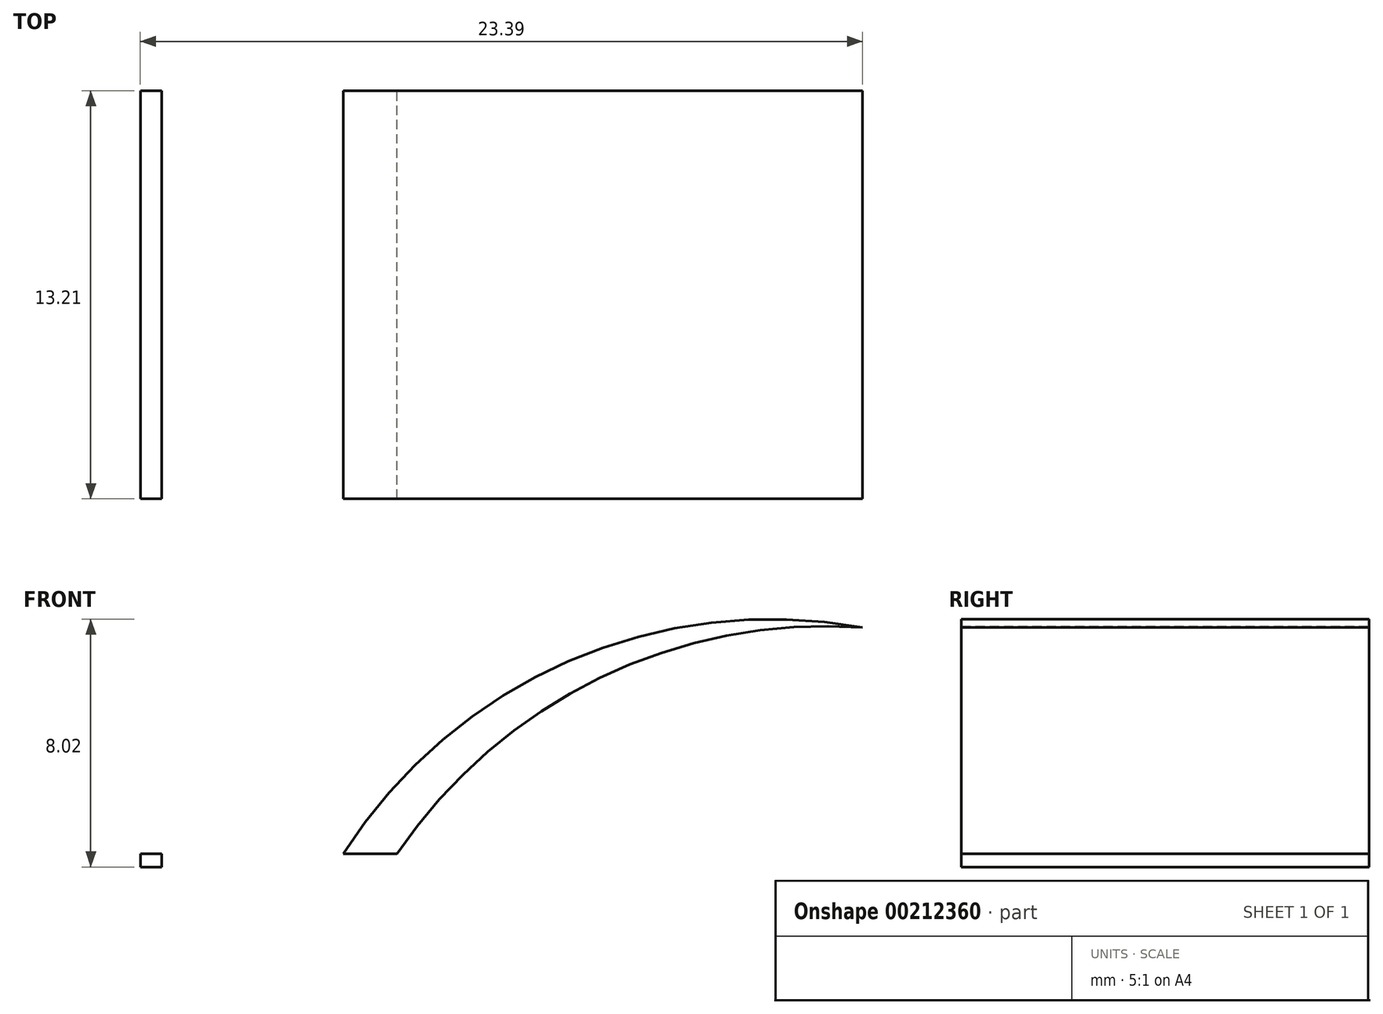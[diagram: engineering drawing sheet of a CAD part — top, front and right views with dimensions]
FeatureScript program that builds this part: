
annotation { "Feature Type Name" : "Feature", "Feature Type Description" : "" }
export const myFeature = defineFeature(function(context is Context, id is Id, definition is map)
    precondition{}
    {
        {
            var Q0;
            Q0=qCreatedBy(makeId("Front.planeOp"),FACE);
            var sketch = newSketch(context, id + "F0", { "sketchPlane" : qUnion([Q0])});
            skLineSegment(sketch, "E0.bottom", {"start": v(0.3, -1.39) * mm, "end": v(-2.54, -1.39) * mm});
            skLineSegment(sketch, "E0.top", {"start": v(0.3, -1.39) * mm, "end": v(-2.54, -1.39) * mm});
            skLineSegment(sketch, "E0.left", {"start": v(0.3, -1.39) * mm, "end": v(0.3, -1.39) * mm});
            skLineSegment(sketch, "E0.right", {"start": v(-2.54, -1.39) * mm, "end": v(-2.54, -1.39) * mm});
            skLineSegment(sketch, "E1", {"start": v(2.17, 2.36) * mm, "end": v(-2.5, 2.36) * mm});
            skLineSegment(sketch, "E2", {"start": v(-2.54, 0.16) * mm, "end": v(-2.54, -1.39) * mm});
            skLineSegment(sketch, "E3.bottom", {"start": v(-32.5, 2.68) * mm, "end": v(-24.88, 2.68) * mm});
            skLineSegment(sketch, "E3.left", {"start": v(-32.5, 2.68) * mm, "end": v(-32.5, 1.16) * mm});
            skArc(sketch, "E4", {"start": v(-9.8, 10) * mm, "mid": v(-18.33, 8.36) * mm, "end": v(-24.88, 2.68) * mm});
            skArc(sketch, "E5", {"start": v(-9.8, 10) * mm, "mid": v(-19.33, 8.9) * mm, "end": v(-26.62, 2.68) * mm});
            skPoint(sketch, "E6.visualSharp", {"position": v(2, 2.36) * mm});
            skArc(sketch, "E6.filletArc", {"start": v(2.43, 1.42) * mm, "mid": v(2.66, 1.99) * mm, "end": v(2.17, 2.36) * mm});
            skLineSegment(sketch, "E7", {"start": v(-32.5, 1.16) * mm, "end": v(-33.42, 1.16) * mm});
            skLineSegment(sketch, "E8", {"start": v(-33.42, 1.16) * mm, "end": v(-33.42, 0.43) * mm});
            skLineSegment(sketch, "E9", {"start": v(-33.2, 2.25) * mm, "end": v(-33.2, 2.68) * mm});
            skLineSegment(sketch, "E10", {"start": v(-33.2, 2.68) * mm, "end": v(-32.5, 2.68) * mm});
            skLineSegment(sketch, "E11", {"start": v(-33.2, 2.25) * mm, "end": v(-32.5, 2.25) * mm});
            skArc(sketch, "E12", {"start": v(1.59, 0.88) * mm, "mid": v(-0.72, 0.69) * mm, "end": v(0.3, -1.39) * mm});
            skLineSegment(sketch, "E13", {"start": v(1.59, 0.88) * mm, "end": v(2.43, 1.42) * mm});
            skPoint(sketch, "E14.center.orphan", {"position": v(0, 0) * mm});
            skLineSegment(sketch, "E15", {"start": v(-24.88, 1.16) * mm, "end": v(-3.54, 1.16) * mm});
            skLineSegment(sketch, "E16", {"start": v(-2.5, 2.36) * mm, "end": v(-24.88, 2.36) * mm});
            skArc(sketch, "E17.filletArc", {"start": v(-2.54, 0.16) * mm, "mid": v(-2.84, 0.86) * mm, "end": v(-3.54, 1.16) * mm});
            skLineSegment(sketch, "E18", {"start": v(-24.88, 2.68) * mm, "end": v(-24.88, 0.43) * mm});
            skLineSegment(sketch, "E19", {"start": v(-24.88, 0.43) * mm, "end": v(-33.42, 0.43) * mm});
            skSolve(sketch);
        }
        {
            var Q0;
            Q0=makeQuery(id+"F0.imprint","IMPRINT",FACE,{"disambiguationData":[TD([[makeQuery(id+"F0.imprint","IMPRINT",EDGE,{"derivedFrom":sQuery(id+"F0.wireOp",EDGE,"E0.top")}),-1.0]])]});
            var Q1;
            {var subQ0=sQuery(id+"F0.wireOp",EDGE,"E7");Q1=makeQuery(id+"F0.imprint","IMPRINT",FACE,{"disambiguationData":[TD([[makeQuery(id+"F0.imprint","IMPRINT",EDGE,{"derivedFrom":subQ0}),1.0]])]});}
            var Q2;
            Q2=makeQuery(id+"F0.imprint","IMPRINT",FACE,{"disambiguationData":[TD([[makeQuery(id+"F0.imprint","IMPRINT",EDGE,{"derivedFrom":sQuery(id+"F0.wireOp",EDGE,"E9")}),-1.0]])]});
            var Q3;
            {var subQ0=sQuery(id+"F0.wireOp",EDGE,"E4");Q3=makeQuery(id+"F0.imprint","IMPRINT",FACE,{"disambiguationData":[TD([[makeQuery(id+"F0.imprint","IMPRINT",EDGE,{"derivedFrom":subQ0}),-1.0]])]});}
            extrude(context, id + "F1", {"entities" : qUnion([Q0, Q1, Q2, Q3]), "depth" : 13.2 * mm});
        }
    });
